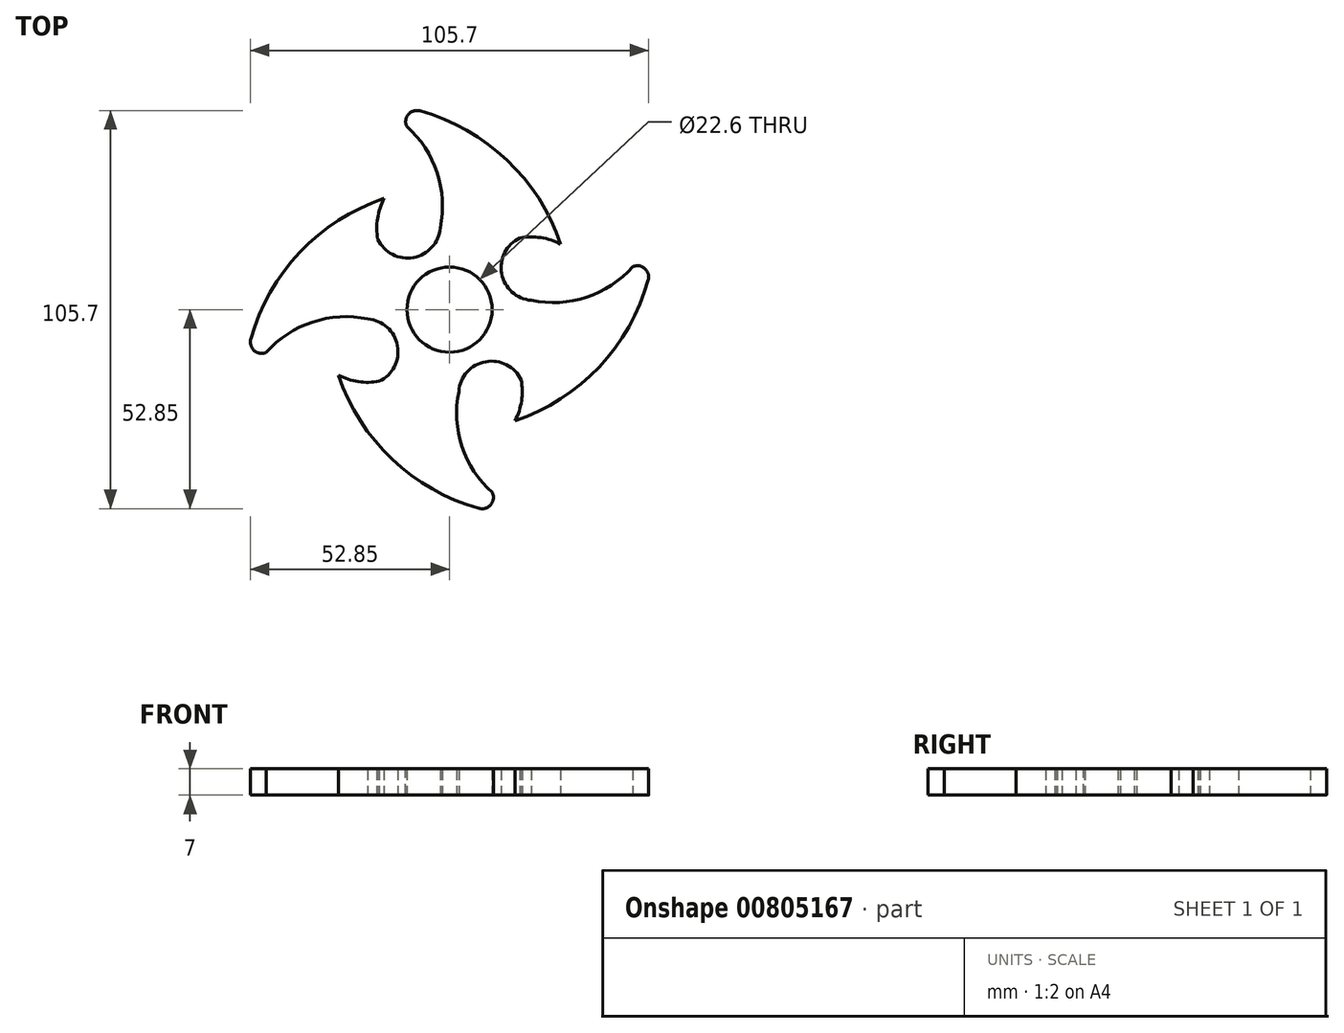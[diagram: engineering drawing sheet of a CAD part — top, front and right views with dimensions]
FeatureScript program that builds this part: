
annotation { "Feature Type Name" : "Feature", "Feature Type Description" : "" }
export const myFeature = defineFeature(function(context is Context, id is Id, definition is map)
    precondition{}
    {
        {
            var Q0;
            Q0=qCreatedBy(makeId("Top.planeOp"),FACE);
            var sketch = newSketch(context, id + "F0", { "sketchPlane" : qUnion([Q0])});
            skArc(sketch, "E0", {"start": v(-17.38, 29.5) * mm, "mid": v(-19.1, 24.22) * mm, "end": v(-19.02, 18.67) * mm});
            skArc(sketch, "E1", {"start": v(-19.02, 18.67) * mm, "mid": v(-9.58, 13.82) * mm, "end": v(-2.47, 21.7) * mm});
            skArc(sketch, "E2", {"start": v(-2.47, 21.7) * mm, "mid": v(-3.3, 36.35) * mm, "end": v(-11.37, 48.6) * mm});
            skArc(sketch, "E3", {"start": v(-11.37, 48.6) * mm, "mid": v(-14.28, 51.65) * mm, "end": v(-17.38, 54.5) * mm});
            skArc(sketch, "E4.3.1", {"start": v(29.5, 17.38) * mm, "mid": v(24.22, 19.1) * mm, "end": v(18.67, 19.02) * mm});
            skArc(sketch, "E4.3.2", {"start": v(18.67, 19.02) * mm, "mid": v(13.82, 9.58) * mm, "end": v(21.7, 2.47) * mm});
            skPoint(sketch, "E4.center", {"position": v(0, 0) * mm});
            skArc(sketch, "E5", {"start": v(29.5, 17.38) * mm, "mid": v(11.56, 42.88) * mm, "end": v(-17.38, 54.5) * mm});
            skCircle(sketch, "E6", {"center": v(0, 0) * mm, "radius": 16.3 * mm});
            skLineSegment(sketch, "E7", {"start": v(-17.38, 29.5) * mm, "end": v(3.23, 29.5) * mm, "construction": true});
            skLineSegment(sketch, "E8", {"start": v(29.5, 17.38) * mm, "end": v(29.5, -4.04) * mm, "construction": true});
            skLineSegment(sketch, "E9", {"start": v(-17.38, 54.5) * mm, "end": v(-17.38, 29.5) * mm, "construction": true});
            skCircle(sketch, "E10", {"center": v(0, 0) * mm, "radius": 11.3 * mm});
            skArc(sketch, "E11.1.0", {"start": v(-29.5, -17.38) * mm, "mid": v(-24.22, -19.1) * mm, "end": v(-18.67, -19.02) * mm});
            skArc(sketch, "E11.1.1", {"start": v(-18.67, -19.02) * mm, "mid": v(-13.82, -9.58) * mm, "end": v(-21.7, -2.47) * mm});
            skArc(sketch, "E11.1.2", {"start": v(-21.7, -2.47) * mm, "mid": v(-36.35, -3.3) * mm, "end": v(-48.6, -11.37) * mm});
            skArc(sketch, "E11.1.3", {"start": v(-48.6, -11.37) * mm, "mid": v(-51.65, -14.28) * mm, "end": v(-54.5, -17.38) * mm});
            skArc(sketch, "E11.1.4", {"start": v(-17.38, 29.5) * mm, "mid": v(-42.88, 11.56) * mm, "end": v(-54.5, -17.38) * mm});
            skArc(sketch, "E11.2.0", {"start": v(17.38, -29.5) * mm, "mid": v(19.1, -24.22) * mm, "end": v(19.02, -18.67) * mm});
            skArc(sketch, "E11.2.2", {"start": v(2.47, -21.7) * mm, "mid": v(3.3, -36.35) * mm, "end": v(11.37, -48.6) * mm});
            skArc(sketch, "E11.2.3", {"start": v(11.37, -48.6) * mm, "mid": v(14.28, -51.65) * mm, "end": v(17.38, -54.5) * mm});
            skArc(sketch, "E11.2.4", {"start": v(-29.5, -17.38) * mm, "mid": v(-11.56, -42.88) * mm, "end": v(17.38, -54.5) * mm});
            skArc(sketch, "E12.8.3.0", {"start": v(21.7, 2.47) * mm, "mid": v(36.35, 3.3) * mm, "end": v(48.6, 11.37) * mm});
            skArc(sketch, "E12.12.3.0", {"start": v(48.6, 11.37) * mm, "mid": v(51.65, 14.28) * mm, "end": v(54.5, 17.38) * mm});
            skArc(sketch, "E12.16.3.0", {"start": v(17.38, -29.5) * mm, "mid": v(42.88, -11.56) * mm, "end": v(54.5, 17.38) * mm});
            skArc(sketch, "E12.20.3.0", {"start": v(19.02, -18.67) * mm, "mid": v(9.58, -13.82) * mm, "end": v(2.47, -21.7) * mm});
            skSolve(sketch);
        }
        {
            var Q0;
            Q0=makeQuery(id+"F0.imprint","IMPRINT",FACE,{"disambiguationData":[TD([[makeQuery(id+"F0.imprint","IMPRINT",EDGE,{"derivedFrom":sQuery(id+"F0.wireOp",EDGE,"E0")}),-1.0]])]});
            var Q1;
            {var subQ0=sQuery(id+"F0.wireOp",EDGE,"E2");Q1=makeQuery(id+"F0.imprint","IMPRINT",FACE,{"disambiguationData":[TD([[makeQuery(id+"F0.imprint","IMPRINT",EDGE,{"derivedFrom":subQ0}),-1.0]])]});}
            var Q2;
            {var subQ5=sQuery(id+"F0.wireOp",EDGE,"E4.1.1");Q2=makeQuery(id+"F0.imprint","IMPRINT",FACE,{"disambiguationData":[TD([[makeQuery(id+"F0.imprint","IMPRINT",EDGE,{"derivedFrom":subQ5}),-1.0]])]});}
            var Q3;
            {var subQ6=sQuery(id+"F0.wireOp",EDGE,"E4.2.1");Q3=makeQuery(id+"F0.imprint","IMPRINT",FACE,{"disambiguationData":[TD([[makeQuery(id+"F0.imprint","IMPRINT",EDGE,{"derivedFrom":subQ6}),-1.0]])]});}
            var Q4;
            Q4=makeQuery(id+"F0.imprint","IMPRINT",FACE,{"disambiguationData":[TD([[makeQuery(id+"F0.imprint","IMPRINT",EDGE,{"derivedFrom":sQuery(id+"F0.wireOp",EDGE,"E10")}),-1.0]])]});
            var Q5;
            {var subQ0=sQuery(id+"F0.wireOp",EDGE,"E11.1.2");Q5=makeQuery(id+"F0.imprint","IMPRINT",FACE,{"disambiguationData":[TD([[makeQuery(id+"F0.imprint","IMPRINT",EDGE,{"derivedFrom":subQ0}),-1.0]])]});}
            var Q6;
            {var subQ5=sQuery(id+"F0.wireOp",EDGE,"E11.2.2");Q6=makeQuery(id+"F0.imprint","IMPRINT",FACE,{"disambiguationData":[TD([[makeQuery(id+"F0.imprint","IMPRINT",EDGE,{"derivedFrom":subQ5}),-1.0]])]});}
            var Q7;
            {var subQ0=sQuery(id+"F0.wireOp",EDGE,"E12.8.3.0");Q7=makeQuery(id+"F0.imprint","IMPRINT",FACE,{"disambiguationData":[TD([[makeQuery(id+"F0.imprint","IMPRINT",EDGE,{"derivedFrom":subQ0}),-1.0]])]});}
            extrude(context, id + "F1", {"entities" : qUnion([Q0, Q1, Q2, Q3, Q4, Q5, Q6, Q7]), "depth" : 7 * mm, "offsetDistance" : 25 * mm});
        }
        {
            var Q0;
            Q0=makeQuery(id+"F1.opExtrude","SWEPT_EDGE",EDGE,{"disambiguationData":[OSD([sQuery(id+"F0.wireOp",EDGE,"E11.1.3"),sQuery(id+"F0.wireOp",EDGE,"E11.1.4")])]});
            var Q1;
            Q1=makeQuery(id+"F1.opExtrude","SWEPT_EDGE",EDGE,{"disambiguationData":[OSD([sQuery(id+"F0.wireOp",EDGE,"E11.2.3"),sQuery(id+"F0.wireOp",EDGE,"E11.2.4")])]});
            var Q2;
            Q2=makeQuery(id+"F1.opExtrude","SWEPT_EDGE",EDGE,{"disambiguationData":[OSD([sQuery(id+"F0.wireOp",EDGE,"E12.12.3.0"),sQuery(id+"F0.wireOp",EDGE,"E12.16.3.0")])]});
            var Q3;
            Q3=makeQuery(id+"F1.opExtrude","SWEPT_EDGE",EDGE,{"disambiguationData":[OSD([sQuery(id+"F0.wireOp",EDGE,"E3"),sQuery(id+"F0.wireOp",EDGE,"E5")])]});
            fillet(context, id + "F2", {"entities" : qUnion([Q0, Q1, Q2, Q3]), "radius" : 3 * mm, "tangentPropagation" : true, "allowEdgeOverflow" : false});
        }
    });
